# Revit family: Faucet_Lavatory-DXV-Oak_Hill-D35155840_Series
name_source: partatom
category: Plumbing Fixtures
units: mm (PartAtom-declared; Revit-internal decimal feet)

## family parameters
Always vertical = No
Cut with Voids When Loaded = No
OmniClass Number = 23.45.55.17
OmniClass Title = Mixing Faucets
Part Type = Normal
Room Calculation Point = No
Round Connector Dimension = Use Diameter
Shared = Yes
Work Plane-Based = Yes

## types (4) — shared parameters
Assembly Code = D2020300
CEC Compliant = Yes
CW Connection = Yes
CWFU = 1.5
CalGreen Compliant = Yes
Cold Water Connection Diameter = 3/8"
Cold Water Connection Radius = 3/16"
Default Elevation = 0"
Description = Widespread Lavatory Faucet
Flow Rate = 1.2 GPM (4.5 L/min.)
HW Connection = Yes
HWFU = 1.5
Height = 5 5/8"
Hot Water Connection Diameter = 0"
Hot Water Connection Radius = 3/16"
Installation Type = Deck Mounted
Length = 6 1/8"
Manufacturer = DXV
Price = Prices may vary. Please consult Manufacturer Representative for most up-to-date price list.
URL = https://www.dxv.com
Vent Connection = No
WFU = 2
Waste Connection = No
Width = 8"

## per-type parameters (varying)
| type | Finish | Material |
| D35155840.100 | Cast Brass-DXV-100-Polished Chrome | Cast Brass-DXV-100-Polished Chrome |
| D35155840.144 | Cast Brass-DXV-144-Brushed Nickel | Cast Brass-DXV-144-Brushed Nickel |
| D35155840.150 | Cast Brass-DXV-150-Platinum Nickel | Cast Brass-DXV-150-Platinum Nickel |
| D35155840.427 | Cast Brass-DXV-427-Satin Brass | Cast Brass-DXV-427-Satin Brass |

note: column(s) folded — value = type name in every type: Model

## geometry (parser evidence)
native form markers: Sweep x2
no freeform markers — native parametric forms only
